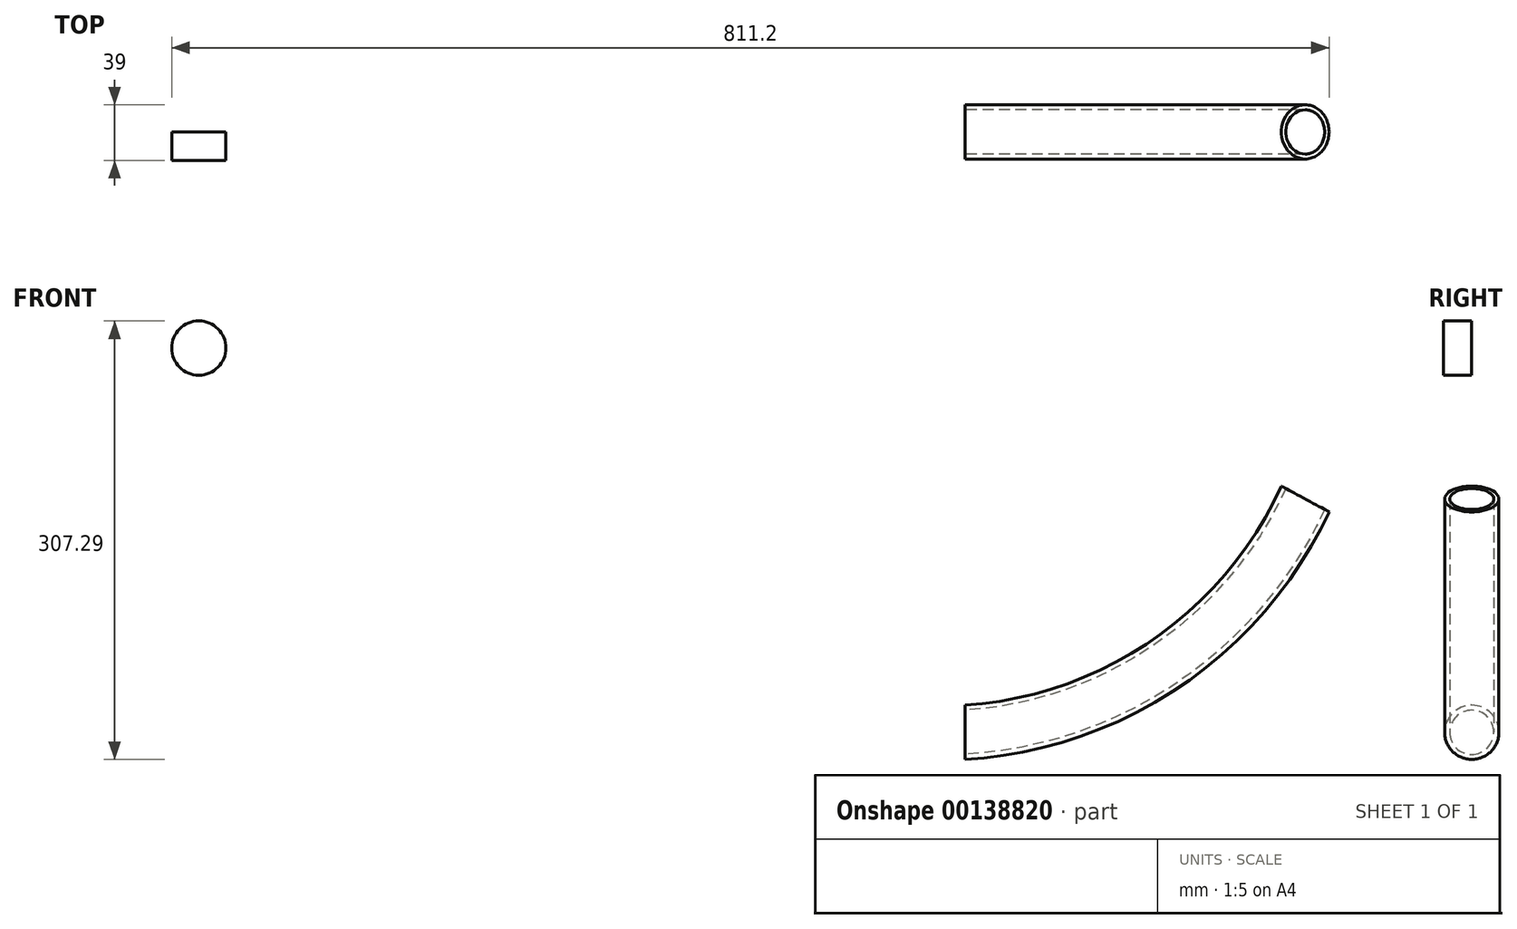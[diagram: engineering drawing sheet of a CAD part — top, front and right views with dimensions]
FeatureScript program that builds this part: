
annotation { "Feature Type Name" : "Feature", "Feature Type Description" : "" }
export const myFeature = defineFeature(function(context is Context, id is Id, definition is map)
    precondition{}
    {
        {
            var Q0;
            Q0=qCreatedBy(makeId("Right.planeOp"),FACE);
            var sketch = newSketch(context, id + "F0", { "sketchPlane" : qUnion([Q0])});
            skCircle(sketch, "E0", {"center": v(0, 0) * mm, "radius": 19 * mm});
            skCircle(sketch, "E1", {"center": v(0, 0) * mm, "radius": 15.5 * mm});
            skSolve(sketch);
        }
        {
            var Q0;
            Q0=qCreatedBy(makeId("Front.planeOp"),FACE);
            var sketch = newSketch(context, id + "F1", { "sketchPlane" : qUnion([Q0])});
            skArc(sketch, "E2", {"start": v(0, 0) * mm, "mid": v(141.8, 48.85) * mm, "end": v(238.51, 163.5) * mm});
            skSolve(sketch);
        }
        {
            var Q0;
            Q0=makeQuery(id+"F0.imprint","IMPRINT",FACE,{"disambiguationData":[TD([[makeQuery(id+"F0.imprint","IMPRINT",EDGE,{"derivedFrom":sQuery(id+"F0.wireOp",EDGE,"E0")}),1.0]])]});
            var Q1;
            Q1=sQuery(id+"F1.wireOp",EDGE,"E2");
            sweep(context, id + "F2", {"profiles" : qUnion([Q0]), "path" : qUnion([Q1])});
        }
        {
            var Q0;
            Q0=qCreatedBy(makeId("Front.planeOp"),FACE);
            var sketch = newSketch(context, id + "F3", { "sketchPlane" : qUnion([Q0])});
            skCircle(sketch, "E3", {"center": v(-536.96, 269.3) * mm, "radius": 19 * mm});
            skSolve(sketch);
        }
        {
            var Q0;
            Q0 = qSketchRegion(id + "F3", true);
            extrude(context, id + "F4", {"entities" : qUnion([Q0]), "depth" : 20 * mm});
        }
    });
